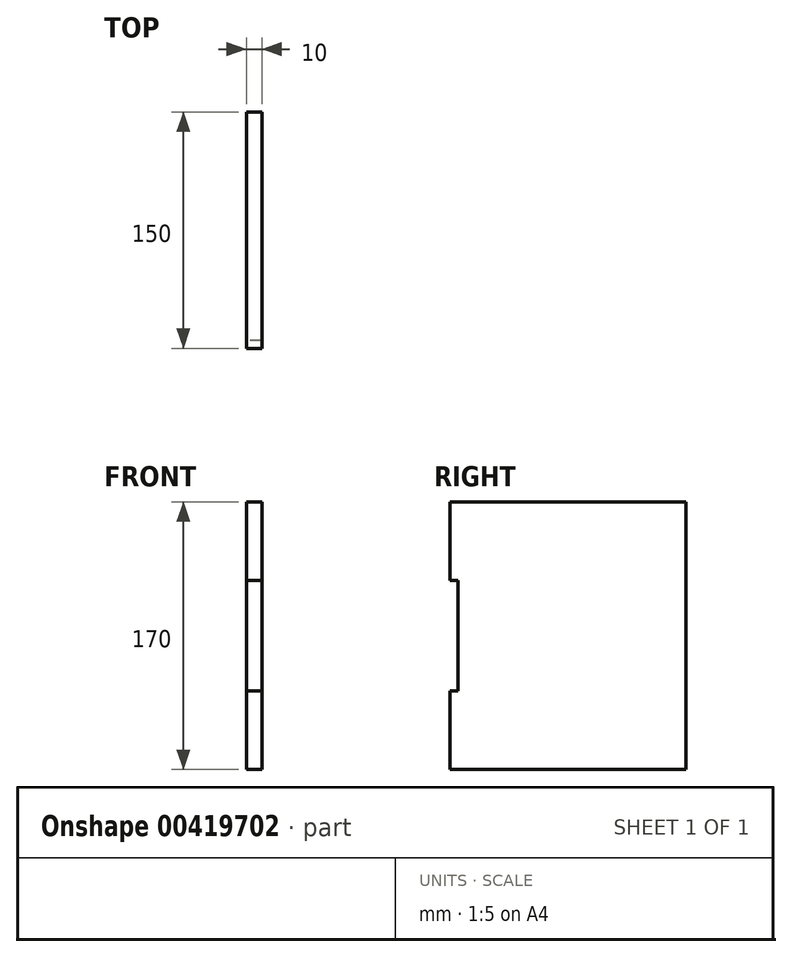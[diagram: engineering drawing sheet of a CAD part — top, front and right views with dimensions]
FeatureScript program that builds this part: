
annotation { "Feature Type Name" : "Feature", "Feature Type Description" : "" }
export const myFeature = defineFeature(function(context is Context, id is Id, definition is map)
    precondition{}
    {
        {
            var Q0;
            Q0=qCreatedBy(makeId("Right.planeOp"),FACE);
            var sketch = newSketch(context, id + "F0", { "sketchPlane" : qUnion([Q0])});
            skLineSegment(sketch, "E0.bottom", {"start": v(111.25, 85) * mm, "end": v(-38.75, 85) * mm});
            skLineSegment(sketch, "E0.top", {"start": v(111.25, -85) * mm, "end": v(-38.75, -85) * mm});
            skLineSegment(sketch, "E0.left", {"start": v(111.25, 85) * mm, "end": v(111.25, -85) * mm});
            skLineSegment(sketch, "E0.right", {"start": v(-38.75, 85) * mm, "end": v(-38.75, 35) * mm});
            skLineSegment(sketch, "E1.bottom", {"start": v(-38.75, 35) * mm, "end": v(-33.75, 35) * mm});
            skLineSegment(sketch, "E1.top", {"start": v(-38.75, -35) * mm, "end": v(-33.75, -35) * mm});
            skLineSegment(sketch, "E1.right", {"start": v(-33.75, 35) * mm, "end": v(-33.75, -35) * mm});
            skLineSegment(sketch, "E2.trimOffspring", {"start": v(-38.75, -35) * mm, "end": v(-38.75, -85) * mm});
            skSolve(sketch);
        }
        {
            var Q0;
            Q0=makeQuery(id+"F0.imprint","IMPRINT",FACE,{"disambiguationData":[TD([[makeQuery(id+"F0.imprint","IMPRINT",EDGE,{"derivedFrom":sQuery(id+"F0.wireOp",EDGE,"E0.bottom")}),1.0]])]});
            extrude(context, id + "F1", {"entities" : qUnion([Q0]), "depth" : 10 * mm});
        }
    });
